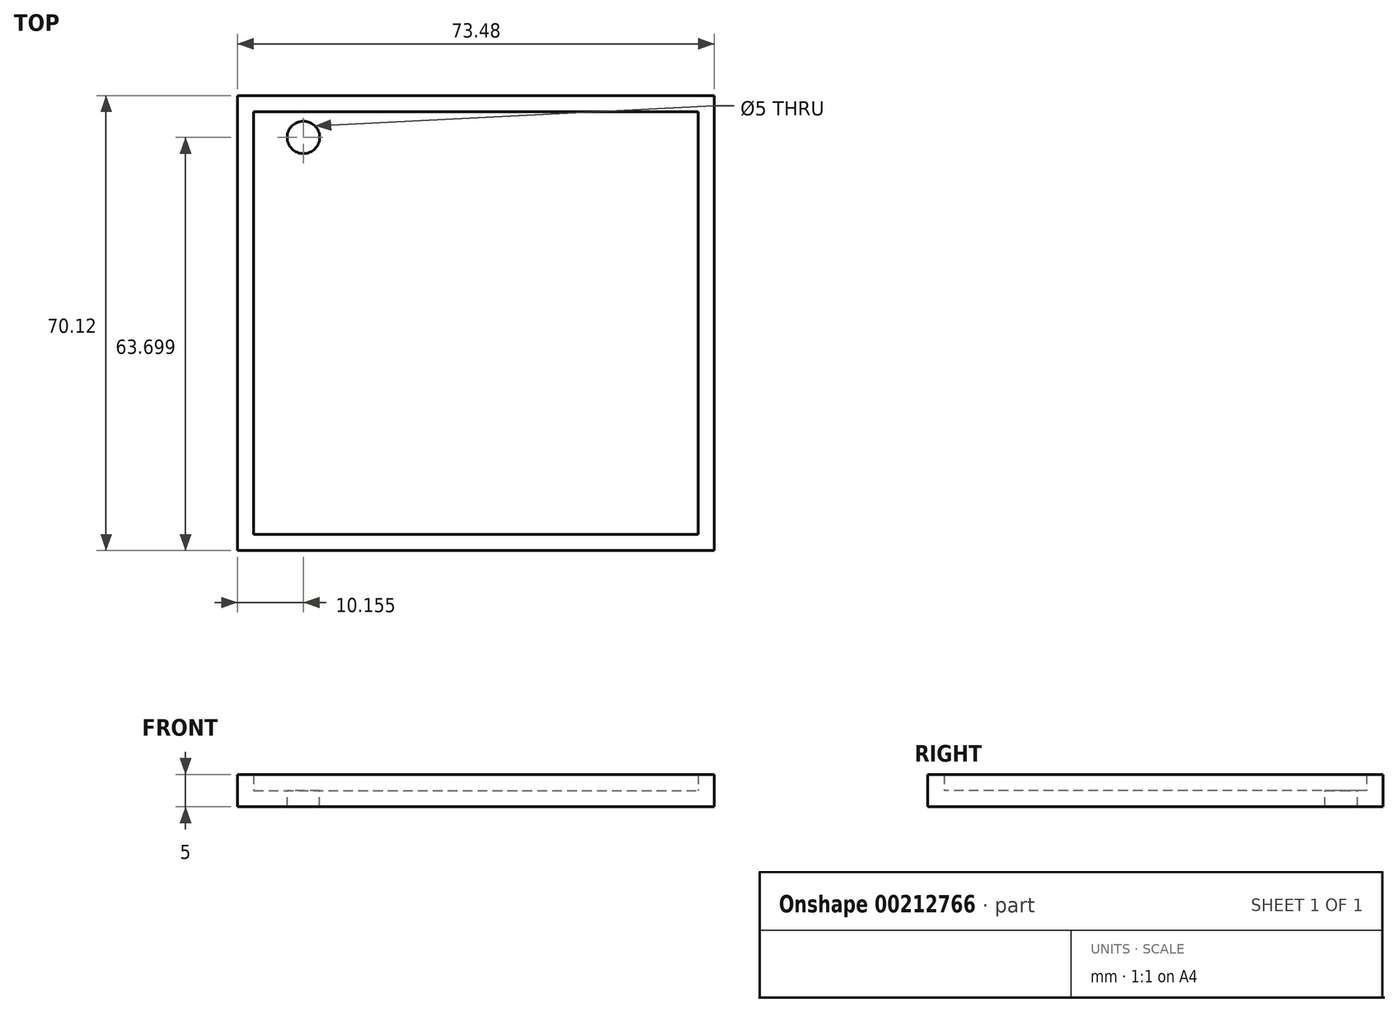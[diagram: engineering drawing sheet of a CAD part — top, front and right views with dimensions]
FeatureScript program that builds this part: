
annotation { "Feature Type Name" : "Feature", "Feature Type Description" : "" }
export const myFeature = defineFeature(function(context is Context, id is Id, definition is map)
    precondition{}
    {
        {
            var Q0;
            Q0=qCreatedBy(makeId("Top.planeOp"),FACE);
            var sketch = newSketch(context, id + "F0", { "sketchPlane" : qUnion([Q0])});
            skLineSegment(sketch, "E0.bottom", {"start": v(0, 0) * mm, "end": v(73.48, 0) * mm});
            skLineSegment(sketch, "E0.top", {"start": v(0, -70.12) * mm, "end": v(73.48, -70.12) * mm});
            skLineSegment(sketch, "E0.left", {"start": v(0, 0) * mm, "end": v(0, -70.12) * mm});
            skLineSegment(sketch, "E0.right", {"start": v(73.48, 0) * mm, "end": v(73.48, -70.12) * mm});
            skSolve(sketch);
        }
        {
            var Q0;
            Q0=makeQuery(id+"F0.imprint","IMPRINT",FACE,{"disambiguationData":[TD([[makeQuery(id+"F0.imprint","IMPRINT",EDGE,{"derivedFrom":sQuery(id+"F0.wireOp",EDGE,"E0.bottom")}),-1.0]])]});
            extrude(context, id + "F1", {"entities" : qUnion([Q0]), "depth" : 5 * mm});
        }
        {
            var Q0;
            Q0=makeQuery(id+"F1.opExtrude","CAP_FACE",FACE,{"disambiguationData":[OSD([sQuery(id+"F0.wireOp",EDGE,"E0.bottom"),sQuery(id+"F0.wireOp",EDGE,"E0.top"),sQuery(id+"F0.wireOp",EDGE,"E0.left"),sQuery(id+"F0.wireOp",EDGE,"E0.right")])],"isStart":false});
            shell(context, id + "F2", {"entities" : qUnion([Q0]), "thickness" : 2.5 * mm});
        }
        {
            var Q0;
            Q0=makeQuery(id+"F2.opShell","OFFSET_FACE",FACE,{"disambiguationData":[OSD([sQuery(id+"F0.wireOp",EDGE,"E0.bottom"),sQuery(id+"F0.wireOp",EDGE,"E0.top"),sQuery(id+"F0.wireOp",EDGE,"E0.left"),sQuery(id+"F0.wireOp",EDGE,"E0.right")])]});
            var sketch = newSketch(context, id + "F3", { "sketchPlane" : qUnion([Q0])});
            skCircle(sketch, "E1", {"center": v(10.15, -6.42) * mm, "radius": 4.4 * mm});
            skPoint(sketch, "E1.first.point", {"position": v(8.18, -2.5) * mm});
            skPoint(sketch, "E1.second.point", {"position": v(9.32, -10.73) * mm});
            skPoint(sketch, "E1.third.point", {"position": v(6.52, -8.88) * mm});
            skSolve(sketch);
        }
        {
            var Q0;
            Q0=sQuery(id+"F3.wireOp",VERTEX,"E1.center");
            var Q1;
            Q1=makeQuery(id+"F1.opExtrude","SWEPT_BODY",BODY,{"disambiguationData":[OSD([sQuery(id+"F0.wireOp",EDGE,"E0.bottom"),sQuery(id+"F0.wireOp",EDGE,"E0.top"),sQuery(id+"F0.wireOp",EDGE,"E0.left"),sQuery(id+"F0.wireOp",EDGE,"E0.right")])]});
            hole(context, id + "F4", {"style" : HoleStyle.SIMPLE, "endStyle" : HoleEndStyle.THROUGH, "holeDiameter" : 5 * mm, "locations" : qUnion([Q0]), "scope" : qUnion([Q1]), "isTappedThrough" : true});
        }
    });
